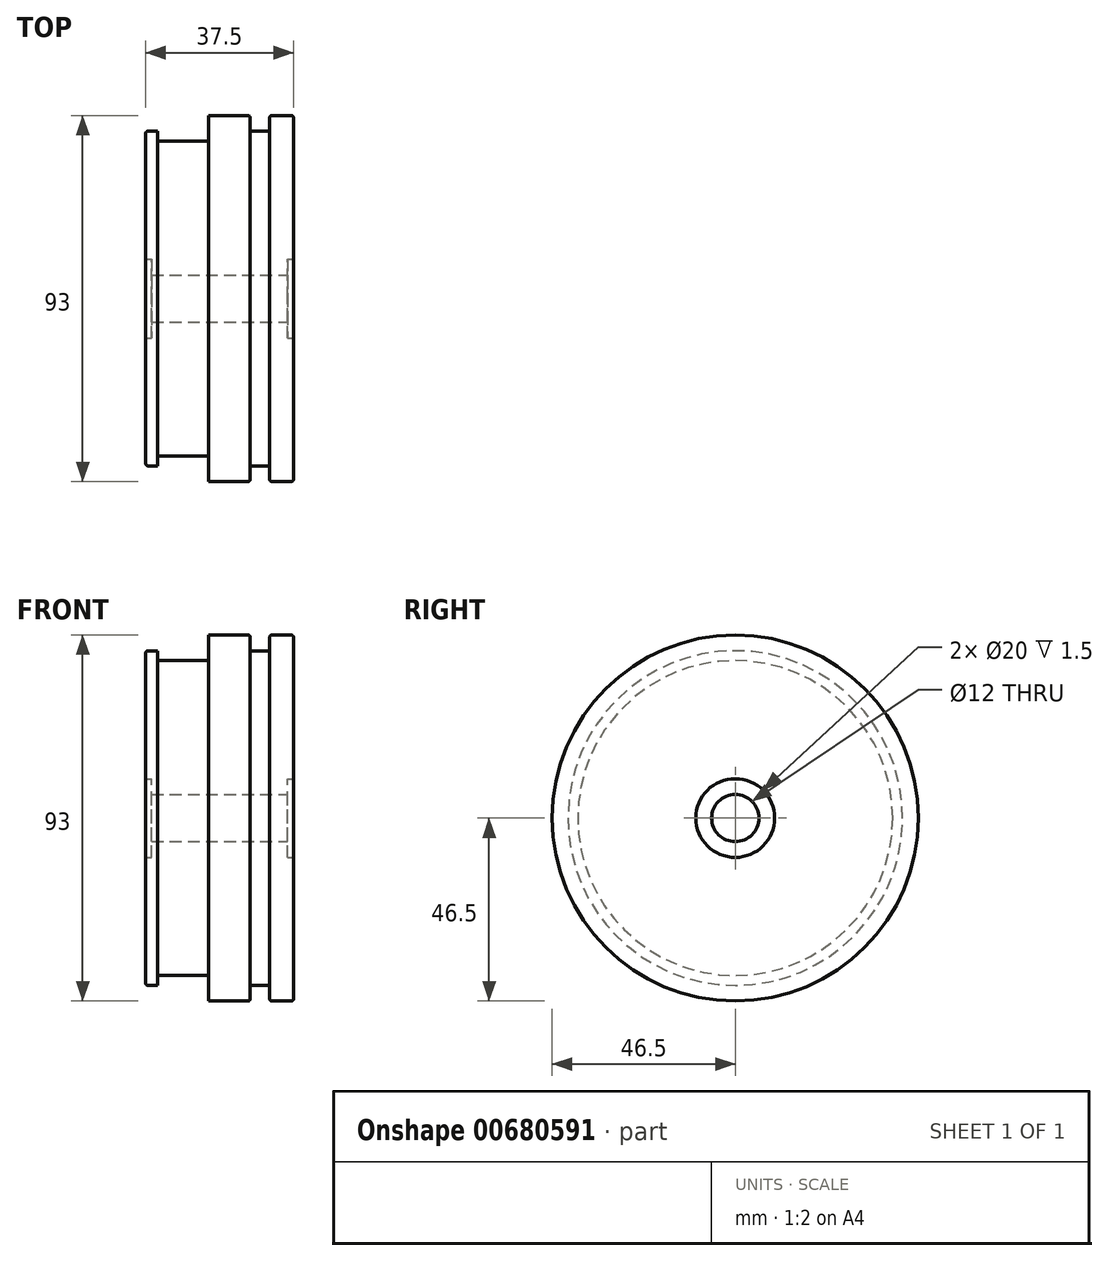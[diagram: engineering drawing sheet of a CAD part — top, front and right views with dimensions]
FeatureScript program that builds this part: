
annotation { "Feature Type Name" : "Feature", "Feature Type Description" : "" }
export const myFeature = defineFeature(function(context is Context, id is Id, definition is map)
    precondition{}
    {
        {
            var Q0;
            Q0=qCreatedBy(makeId("Front.planeOp"),FACE);
            var sketch = newSketch(context, id + "F0", { "sketchPlane" : qUnion([Q0])});
            skLineSegment(sketch, "E0", {"start": v(0, 10) * mm, "end": v(0, 42) * mm});
            skLineSegment(sketch, "E1", {"start": v(0.5, 42.5) * mm, "end": v(3, 42.5) * mm});
            skLineSegment(sketch, "E2", {"start": v(3, 42.5) * mm, "end": v(3, 40) * mm});
            skLineSegment(sketch, "E3", {"start": v(3, 40) * mm, "end": v(16, 40) * mm});
            skLineSegment(sketch, "E4", {"start": v(16, 40) * mm, "end": v(16, 46.5) * mm});
            skLineSegment(sketch, "E5", {"start": v(16, 46.5) * mm, "end": v(26, 46.5) * mm});
            skLineSegment(sketch, "E6", {"start": v(37.5, 46) * mm, "end": v(37.5, 10) * mm});
            skLineSegment(sketch, "E7", {"start": v(37.5, 0) * mm, "end": v(0, 0) * mm});
            skLineSegment(sketch, "E8.0", {"start": v(31.5, 46) * mm, "end": v(31.5, 42.5) * mm});
            skLineSegment(sketch, "E9.0", {"start": v(26.5, 46) * mm, "end": v(26.5, 42.5) * mm});
            skLineSegment(sketch, "E10.0", {"start": v(26.5, 42.5) * mm, "end": v(31.5, 42.5) * mm});
            skLineSegment(sketch, "E11.trimOffspring", {"start": v(32, 46.5) * mm, "end": v(37, 46.5) * mm});
            skLineSegment(sketch, "E12.0", {"start": v(36, 6) * mm, "end": v(1.5, 6) * mm});
            skLineSegment(sketch, "E13.0", {"start": v(37.5, 10) * mm, "end": v(36, 10) * mm});
            skLineSegment(sketch, "E14.0", {"start": v(36, 10) * mm, "end": v(36, 6) * mm});
            skLineSegment(sketch, "E15", {"start": v(0, 10) * mm, "end": v(1.5, 10) * mm});
            skLineSegment(sketch, "E16", {"start": v(1.5, 10) * mm, "end": v(1.5, 6) * mm});
            skPoint(sketch, "E17.visualSharp", {"position": v(26.5, 46.5) * mm});
            skArc(sketch, "E17.filletArc", {"start": v(26.5, 46) * mm, "mid": v(26.35, 46.35) * mm, "end": v(26, 46.5) * mm});
            skPoint(sketch, "E18.visualSharp", {"position": v(31.5, 46.5) * mm});
            skArc(sketch, "E18.filletArc", {"start": v(32, 46.5) * mm, "mid": v(31.65, 46.35) * mm, "end": v(31.5, 46) * mm});
            skPoint(sketch, "E19.visualSharp", {"position": v(37.5, 46.5) * mm});
            skArc(sketch, "E19.filletArc", {"start": v(37.5, 46) * mm, "mid": v(37.35, 46.35) * mm, "end": v(37, 46.5) * mm});
            skPoint(sketch, "E20.visualSharp", {"position": v(0, 42.5) * mm});
            skArc(sketch, "E20.filletArc", {"start": v(0.5, 42.5) * mm, "mid": v(0.15, 42.35) * mm, "end": v(0, 42) * mm});
            skSolve(sketch);
        }
        {
            var Q0;
            Q0 = qSketchRegion(id + "F0", true);
            var Q1;
            Q1 = qConstructionFilter(qBodyType(qCreatedBy(id + "F0" ,EDGE), BodyType.WIRE), ConstructionObject.NO);
            var Q2;
            Q2=sQuery(id+"F0.wireOp",EDGE,"E7");
            revolve(context, id + "F1", {"entities" : qUnion([Q0]), "surfaceEntities" : qUnion([Q1]), "axis" : qUnion([Q2]), "revolveType" : RevolveType.FULL});
        }
    });
